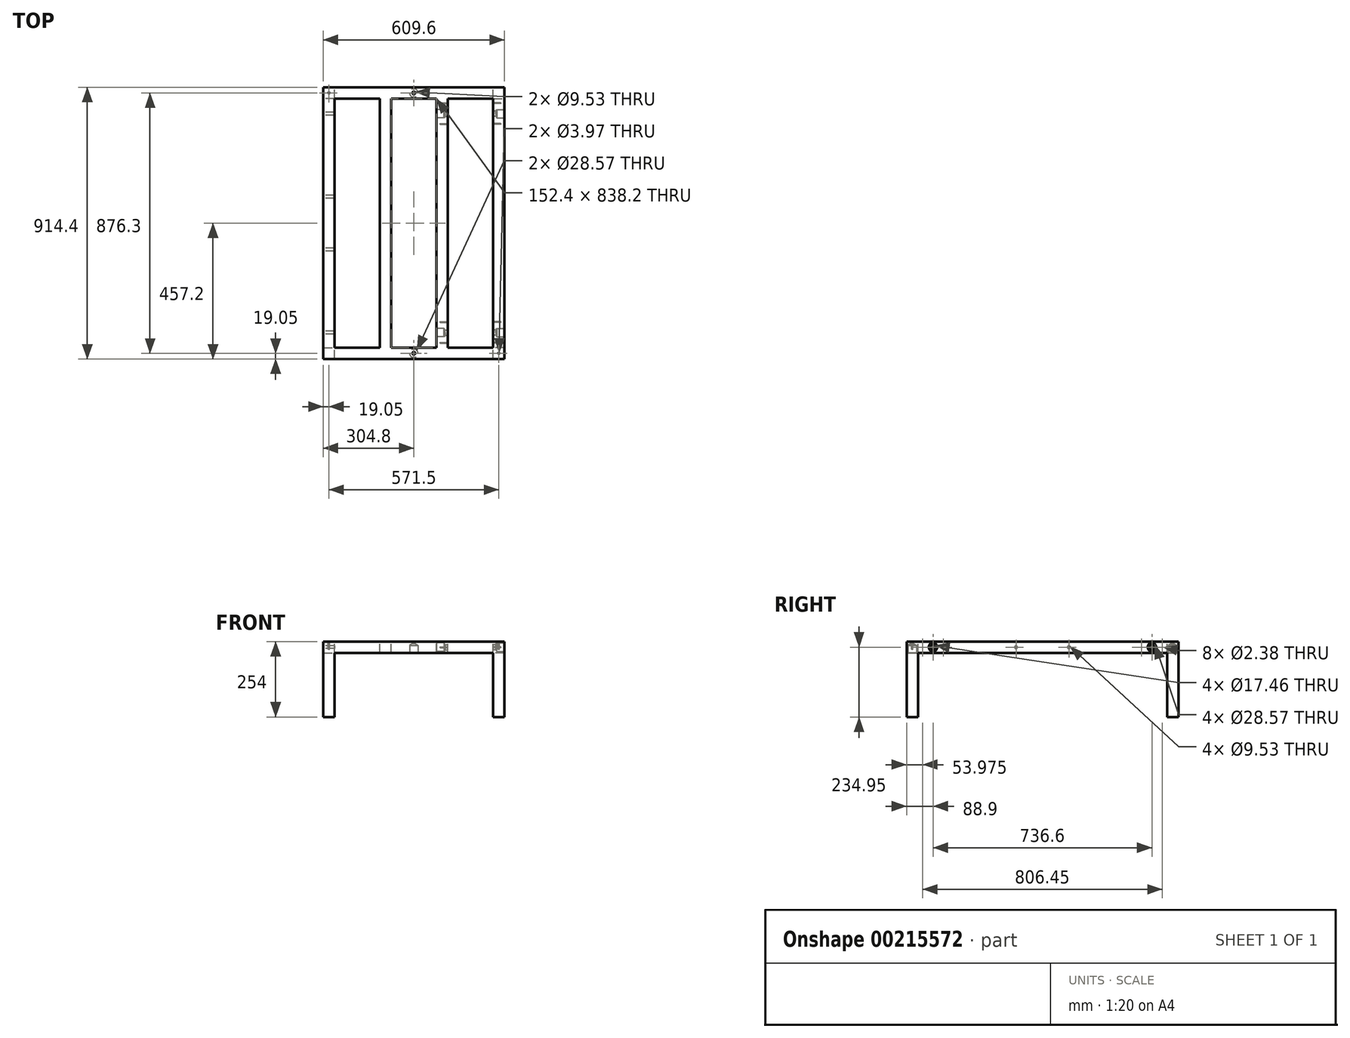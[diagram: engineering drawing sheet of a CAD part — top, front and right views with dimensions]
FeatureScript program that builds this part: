
annotation { "Feature Type Name" : "Feature", "Feature Type Description" : "" }
export const myFeature = defineFeature(function(context is Context, id is Id, definition is map)
    precondition{}
    {
        {
            var Q0;
            Q0=qCreatedBy(makeId("Top.planeOp"),FACE);
            var sketch = newSketch(context, id + "F0", { "sketchPlane" : qUnion([Q0])});
            skLineSegment(sketch, "E0.bottom", {"start": v(304.8, 457.2) * mm, "end": v(-304.8, 457.2) * mm});
            skLineSegment(sketch, "E0.top", {"start": v(304.8, -457.2) * mm, "end": v(-304.8, -457.2) * mm});
            skLineSegment(sketch, "E0.left", {"start": v(304.8, 457.2) * mm, "end": v(304.8, -457.2) * mm});
            skLineSegment(sketch, "E0.right", {"start": v(-304.8, 457.2) * mm, "end": v(-304.8, -457.2) * mm});
            skPoint(sketch, "E0.middle", {"position": v(0, 0) * mm});
            skLineSegment(sketch, "E1.bottom", {"start": v(266.7, 419.1) * mm, "end": v(114.3, 419.1) * mm});
            skLineSegment(sketch, "E1.top", {"start": v(266.7, -419.1) * mm, "end": v(114.3, -419.1) * mm});
            skLineSegment(sketch, "E1.left", {"start": v(266.7, 419.1) * mm, "end": v(266.7, -419.1) * mm});
            skLineSegment(sketch, "E1.right", {"start": v(-266.7, 419.1) * mm, "end": v(-266.7, -419.1) * mm});
            skLineSegment(sketch, "E2.0", {"start": v(-114.3, 419.1) * mm, "end": v(-114.3, -419.1) * mm});
            skLineSegment(sketch, "E3.0", {"start": v(-76.2, 419.1) * mm, "end": v(-76.2, -419.1) * mm});
            skLineSegment(sketch, "E4.0", {"start": v(76.2, 419.1) * mm, "end": v(76.2, -419.1) * mm});
            skLineSegment(sketch, "E5.0", {"start": v(114.3, 419.1) * mm, "end": v(114.3, -419.1) * mm});
            skLineSegment(sketch, "E6.trimOffspring", {"start": v(-114.3, 419.1) * mm, "end": v(-266.7, 419.1) * mm});
            skLineSegment(sketch, "E7.trimOffspring", {"start": v(76.2, 419.1) * mm, "end": v(-76.2, 419.1) * mm});
            skLineSegment(sketch, "E8.trimOffspring", {"start": v(-114.3, -419.1) * mm, "end": v(-266.7, -419.1) * mm});
            skLineSegment(sketch, "E9.trimOffspring", {"start": v(76.2, -419.1) * mm, "end": v(-76.2, -419.1) * mm});
            skSolve(sketch);
        }
        {
            var Q0;
            Q0=qSketchRegion(id+"F0",true);
            extrude(context, id + "F1", {"entities" : qUnion([Q0]), "oppositeDirection" : true, "depth" : 38.1 * mm});
        }
        {
            var Q0;
            Q0=makeQuery(id+"F1.opExtrude","CAP_FACE",FACE,{"disambiguationData":[OSD([sQuery(id+"F0.wireOp",EDGE,"E0.bottom"),sQuery(id+"F0.wireOp",EDGE,"E0.top"),sQuery(id+"F0.wireOp",EDGE,"E0.left"),sQuery(id+"F0.wireOp",EDGE,"E0.right"),sQuery(id+"F0.wireOp",EDGE,"E1.bottom"),sQuery(id+"F0.wireOp",EDGE,"E1.top"),sQuery(id+"F0.wireOp",EDGE,"E1.left"),sQuery(id+"F0.wireOp",EDGE,"E1.right"),sQuery(id+"F0.wireOp",EDGE,"E2.0"),sQuery(id+"F0.wireOp",EDGE,"E3.0"),sQuery(id+"F0.wireOp",EDGE,"E4.0"),sQuery(id+"F0.wireOp",EDGE,"E5.0"),sQuery(id+"F0.wireOp",EDGE,"E6.trimOffspring"),sQuery(id+"F0.wireOp",EDGE,"E7.trimOffspring"),sQuery(id+"F0.wireOp",EDGE,"E8.trimOffspring"),sQuery(id+"F0.wireOp",EDGE,"E9.trimOffspring")])],"isStart":false});
            var sketch = newSketch(context, id + "F2", { "sketchPlane" : qUnion([Q0])});
            skLineSegment(sketch, "E10.bottom", {"start": v(-266.7, -419.1) * mm, "end": v(-304.8, -419.1) * mm});
            skLineSegment(sketch, "E10.top", {"start": v(-266.7, -457.2) * mm, "end": v(-304.8, -457.2) * mm});
            skLineSegment(sketch, "E10.left", {"start": v(-266.7, -419.1) * mm, "end": v(-266.7, -457.2) * mm});
            skLineSegment(sketch, "E10.right", {"start": v(-304.8, -419.1) * mm, "end": v(-304.8, -457.2) * mm});
            skLineSegment(sketch, "E11.bottom", {"start": v(266.7, -419.1) * mm, "end": v(304.8, -419.1) * mm});
            skLineSegment(sketch, "E11.top", {"start": v(266.7, -457.2) * mm, "end": v(304.8, -457.2) * mm});
            skLineSegment(sketch, "E11.left", {"start": v(266.7, -419.1) * mm, "end": v(266.7, -457.2) * mm});
            skLineSegment(sketch, "E11.right", {"start": v(304.8, -419.1) * mm, "end": v(304.8, -457.2) * mm});
            skLineSegment(sketch, "E12.bottom", {"start": v(-304.8, 457.2) * mm, "end": v(-266.7, 457.2) * mm});
            skLineSegment(sketch, "E12.top", {"start": v(-304.8, 419.1) * mm, "end": v(-266.7, 419.1) * mm});
            skLineSegment(sketch, "E12.left", {"start": v(-304.8, 457.2) * mm, "end": v(-304.8, 419.1) * mm});
            skLineSegment(sketch, "E12.right", {"start": v(-266.7, 457.2) * mm, "end": v(-266.7, 419.1) * mm});
            skLineSegment(sketch, "E13.bottom", {"start": v(304.8, 457.2) * mm, "end": v(266.7, 457.2) * mm});
            skLineSegment(sketch, "E13.top", {"start": v(304.8, 419.1) * mm, "end": v(266.7, 419.1) * mm});
            skLineSegment(sketch, "E13.left", {"start": v(304.8, 457.2) * mm, "end": v(304.8, 419.1) * mm});
            skLineSegment(sketch, "E13.right", {"start": v(266.7, 457.2) * mm, "end": v(266.7, 419.1) * mm});
            skSolve(sketch);
        }
        {
            var Q0;
            Q0=makeQuery(id+"F2.imprint","IMPRINT",FACE,{"disambiguationData":[TD([[makeQuery(id+"F2.imprint","IMPRINT",EDGE,{"derivedFrom":sQuery(id+"F2.wireOp",EDGE,"E10.bottom")}),1.0]])]});
            var Q1;
            Q1=makeQuery(id+"F2.imprint","IMPRINT",FACE,{"disambiguationData":[TD([[makeQuery(id+"F2.imprint","IMPRINT",EDGE,{"derivedFrom":sQuery(id+"F2.wireOp",EDGE,"E11.bottom")}),-1.0]])]});
            var Q2;
            Q2=makeQuery(id+"F2.imprint","IMPRINT",FACE,{"disambiguationData":[TD([[makeQuery(id+"F2.imprint","IMPRINT",EDGE,{"derivedFrom":sQuery(id+"F2.wireOp",EDGE,"E13.bottom")}),1.0]])]});
            var Q3;
            Q3=makeQuery(id+"F2.imprint","IMPRINT",FACE,{"disambiguationData":[TD([[makeQuery(id+"F2.imprint","IMPRINT",EDGE,{"derivedFrom":sQuery(id+"F2.wireOp",EDGE,"E12.bottom")}),1.0]])]});
            extrude(context, id + "F3", {"entities" : qUnion([Q0, Q1, Q2, Q3]), "operationType" : NewBodyOperationType.ADD, "depth" : 215.9 * mm});
        }
        {
            var Q0;
            Q0=makeQuery(id+"F3.boolean.opBoolean","MERGE",FACE,{"derivedFrom":[makeQuery(id+"F1.opExtrude","SWEPT_FACE",FACE,{"disambiguationData":[OSD([sQuery(id+"F0.wireOp",EDGE,"E0.left")])]}),makeQuery(id+"F3.opExtrude","SWEPT_FACE",FACE,{"disambiguationData":[OSD([sQuery(id+"F2.wireOp",EDGE,"E11.right")])]}),makeQuery(id+"F3.opExtrude","SWEPT_FACE",FACE,{"disambiguationData":[OSD([sQuery(id+"F2.wireOp",EDGE,"E13.left")])]})]});
            var sketch = newSketch(context, id + "F4", { "sketchPlane" : qUnion([Q0])});
            skPoint(sketch, "E14", {"position": v(368.3, -19.05) * mm});
            skPoint(sketch, "E15", {"position": v(-368.3, -19.05) * mm});
            skPoint(sketch, "E16", {"position": v(-200.65, 261.37) * mm});
            skSolve(sketch);
        }
        {
            var Q0;
            Q0=makeQuery(id+"F1.opExtrude","SWEPT_FACE",FACE,{"disambiguationData":[OSD([sQuery(id+"F0.wireOp",EDGE,"E5.0")])]});
            var sketch = newSketch(context, id + "F5", { "sketchPlane" : qUnion([Q0])});
            skPoint(sketch, "E17.0", {"position": v(368.3, -19.05) * mm});
            skPoint(sketch, "E18.0", {"position": v(-368.3, -19.05) * mm});
            skSolve(sketch);
        }
        {
            var Q0;
            Q0=makeQuery(id+"F3.boolean.opBoolean","MERGE",FACE,{"derivedFrom":[makeQuery(id+"F1.opExtrude","SWEPT_FACE",FACE,{"disambiguationData":[OSD([sQuery(id+"F0.wireOp",EDGE,"E0.right")])]}),makeQuery(id+"F3.opExtrude","SWEPT_FACE",FACE,{"disambiguationData":[OSD([sQuery(id+"F2.wireOp",EDGE,"E10.right")])]}),makeQuery(id+"F3.opExtrude","SWEPT_FACE",FACE,{"disambiguationData":[OSD([sQuery(id+"F2.wireOp",EDGE,"E12.left")])]})]});
            var sketch = newSketch(context, id + "F6", { "sketchPlane" : qUnion([Q0])});
            skPoint(sketch, "E19.0", {"position": v(-368.3, -19.05) * mm});
            skPoint(sketch, "E20.0", {"position": v(-88.9, -19.05) * mm});
            skPoint(sketch, "E21.0", {"position": v(88.9, -19.05) * mm});
            skPoint(sketch, "E22.0", {"position": v(368.3, -19.05) * mm});
            skSolve(sketch);
        }
        {
            var Q0;
            Q0=makeQuery(id+"F1.opExtrude","SWEPT_FACE",FACE,{"disambiguationData":[OSD([sQuery(id+"F0.wireOp",EDGE,"E1.left")])]});
            var sketch = newSketch(context, id + "F7", { "sketchPlane" : qUnion([Q0])});
            skPoint(sketch, "E23.0", {"position": v(-368.3, -19.05) * mm});
            skPoint(sketch, "E24.0", {"position": v(368.3, -19.05) * mm});
            skPoint(sketch, "E25", {"position": v(403.23, -19.05) * mm});
            skPoint(sketch, "E26", {"position": v(333.38, -19.05) * mm});
            skLineSegment(sketch, "E27", {"start": v(368.3, -19.05) * mm, "end": v(368.3, 30.08) * mm, "construction": true});
            skPoint(sketch, "E28", {"position": v(-333.38, -19.05) * mm});
            skPoint(sketch, "E29", {"position": v(-403.23, -19.05) * mm});
            skLineSegment(sketch, "E30", {"start": v(-368.3, -19.05) * mm, "end": v(-368.3, 29.6) * mm, "construction": true});
            skSolve(sketch);
        }
        {
            var Q0;
            Q0=sQuery(id+"F4.wireOp",VERTEX,"E14");
            var Q1;
            Q1=sQuery(id+"F4.wireOp",VERTEX,"E15");
            var Q2;
            Q2=makeQuery(id+"F1.opExtrude","SWEPT_BODY",BODY,{"disambiguationData":[OSD([sQuery(id+"F0.wireOp",EDGE,"E0.bottom"),sQuery(id+"F0.wireOp",EDGE,"E0.top"),sQuery(id+"F0.wireOp",EDGE,"E0.left"),sQuery(id+"F0.wireOp",EDGE,"E0.right"),sQuery(id+"F0.wireOp",EDGE,"E1.bottom"),sQuery(id+"F0.wireOp",EDGE,"E1.top"),sQuery(id+"F0.wireOp",EDGE,"E1.left"),sQuery(id+"F0.wireOp",EDGE,"E1.right"),sQuery(id+"F0.wireOp",EDGE,"E2.0"),sQuery(id+"F0.wireOp",EDGE,"E3.0"),sQuery(id+"F0.wireOp",EDGE,"E4.0"),sQuery(id+"F0.wireOp",EDGE,"E5.0"),sQuery(id+"F0.wireOp",EDGE,"E6.trimOffspring"),sQuery(id+"F0.wireOp",EDGE,"E7.trimOffspring"),sQuery(id+"F0.wireOp",EDGE,"E8.trimOffspring"),sQuery(id+"F0.wireOp",EDGE,"E9.trimOffspring")])]});
            hole(context, id + "F8", {"style" : HoleStyle.SIMPLE, "endStyle" : HoleEndStyle.BLIND, "holeDiameter" : 28.57 * mm, "holeDepth" : 25.4 * mm, "locations" : qUnion([Q0, Q1]), "scope" : qUnion([Q2])});
        }
        {
            var Q0;
            Q0=sQuery(id+"F5.wireOp",VERTEX,"E17.0");
            var Q1;
            Q1=sQuery(id+"F5.wireOp",VERTEX,"E18.0");
            var Q2;
            Q2=makeQuery(id+"F1.opExtrude","SWEPT_BODY",BODY,{"disambiguationData":[OSD([sQuery(id+"F0.wireOp",EDGE,"E0.bottom"),sQuery(id+"F0.wireOp",EDGE,"E0.top"),sQuery(id+"F0.wireOp",EDGE,"E0.left"),sQuery(id+"F0.wireOp",EDGE,"E0.right"),sQuery(id+"F0.wireOp",EDGE,"E1.bottom"),sQuery(id+"F0.wireOp",EDGE,"E1.top"),sQuery(id+"F0.wireOp",EDGE,"E1.left"),sQuery(id+"F0.wireOp",EDGE,"E1.right"),sQuery(id+"F0.wireOp",EDGE,"E2.0"),sQuery(id+"F0.wireOp",EDGE,"E3.0"),sQuery(id+"F0.wireOp",EDGE,"E4.0"),sQuery(id+"F0.wireOp",EDGE,"E5.0"),sQuery(id+"F0.wireOp",EDGE,"E6.trimOffspring"),sQuery(id+"F0.wireOp",EDGE,"E7.trimOffspring"),sQuery(id+"F0.wireOp",EDGE,"E8.trimOffspring"),sQuery(id+"F0.wireOp",EDGE,"E9.trimOffspring")])]});
            hole(context, id + "F9", {"style" : HoleStyle.SIMPLE, "endStyle" : HoleEndStyle.BLIND, "holeDiameter" : 17.46 * mm, "holeDepth" : 25.4 * mm, "locations" : qUnion([Q0, Q1]), "scope" : qUnion([Q2])});
        }
        {
            var Q0;
            Q0=sQuery(id+"F7.wireOp",VERTEX,"E23.0");
            var Q1;
            Q1=sQuery(id+"F7.wireOp",VERTEX,"E24.0");
            var Q2;
            Q2=makeQuery(id+"F1.opExtrude","SWEPT_BODY",BODY,{"disambiguationData":[OSD([sQuery(id+"F0.wireOp",EDGE,"E0.bottom"),sQuery(id+"F0.wireOp",EDGE,"E0.top"),sQuery(id+"F0.wireOp",EDGE,"E0.left"),sQuery(id+"F0.wireOp",EDGE,"E0.right"),sQuery(id+"F0.wireOp",EDGE,"E1.bottom"),sQuery(id+"F0.wireOp",EDGE,"E1.top"),sQuery(id+"F0.wireOp",EDGE,"E1.left"),sQuery(id+"F0.wireOp",EDGE,"E1.right"),sQuery(id+"F0.wireOp",EDGE,"E2.0"),sQuery(id+"F0.wireOp",EDGE,"E3.0"),sQuery(id+"F0.wireOp",EDGE,"E4.0"),sQuery(id+"F0.wireOp",EDGE,"E5.0"),sQuery(id+"F0.wireOp",EDGE,"E6.trimOffspring"),sQuery(id+"F0.wireOp",EDGE,"E7.trimOffspring"),sQuery(id+"F0.wireOp",EDGE,"E8.trimOffspring"),sQuery(id+"F0.wireOp",EDGE,"E9.trimOffspring")])]});
            hole(context, id + "F10", {"style" : HoleStyle.SIMPLE, "endStyle" : HoleEndStyle.BLIND, "holeDiameter" : 17.46 * mm, "holeDepth" : 25.4 * mm, "locations" : qUnion([Q0, Q1]), "scope" : qUnion([Q2])});
        }
        {
            var Q0;
            Q0=makeQuery(id+"F1.opExtrude","SWEPT_FACE",FACE,{"disambiguationData":[OSD([sQuery(id+"F0.wireOp",EDGE,"E4.0")])]});
            var sketch = newSketch(context, id + "F11", { "sketchPlane" : qUnion([Q0])});
            skPoint(sketch, "E31.0", {"position": v(-368.3, -19.05) * mm});
            skPoint(sketch, "E32.0", {"position": v(368.3, -19.05) * mm});
            skSolve(sketch);
        }
        {
            var Q0;
            Q0=sQuery(id+"F11.wireOp",VERTEX,"E31.0");
            var Q1;
            Q1=sQuery(id+"F11.wireOp",VERTEX,"E32.0");
            var Q2;
            Q2=makeQuery(id+"F1.opExtrude","SWEPT_BODY",BODY,{"disambiguationData":[OSD([sQuery(id+"F0.wireOp",EDGE,"E0.bottom"),sQuery(id+"F0.wireOp",EDGE,"E0.top"),sQuery(id+"F0.wireOp",EDGE,"E0.left"),sQuery(id+"F0.wireOp",EDGE,"E0.right"),sQuery(id+"F0.wireOp",EDGE,"E1.bottom"),sQuery(id+"F0.wireOp",EDGE,"E1.top"),sQuery(id+"F0.wireOp",EDGE,"E1.left"),sQuery(id+"F0.wireOp",EDGE,"E1.right"),sQuery(id+"F0.wireOp",EDGE,"E2.0"),sQuery(id+"F0.wireOp",EDGE,"E3.0"),sQuery(id+"F0.wireOp",EDGE,"E4.0"),sQuery(id+"F0.wireOp",EDGE,"E5.0"),sQuery(id+"F0.wireOp",EDGE,"E6.trimOffspring"),sQuery(id+"F0.wireOp",EDGE,"E7.trimOffspring"),sQuery(id+"F0.wireOp",EDGE,"E8.trimOffspring"),sQuery(id+"F0.wireOp",EDGE,"E9.trimOffspring")])]});
            hole(context, id + "F12", {"style" : HoleStyle.SIMPLE, "endStyle" : HoleEndStyle.BLIND, "holeDiameter" : 28.57 * mm, "holeDepth" : 25.4 * mm, "locations" : qUnion([Q0, Q1]), "scope" : qUnion([Q2])});
        }
        {
            var Q0;
            Q0=sQuery(id+"F6.wireOp",VERTEX,"E19.0");
            var Q1;
            Q1=sQuery(id+"F6.wireOp",VERTEX,"E20.0");
            var Q2;
            Q2=sQuery(id+"F6.wireOp",VERTEX,"E21.0");
            var Q3;
            Q3=sQuery(id+"F6.wireOp",VERTEX,"E22.0");
            var Q4;
            Q4=makeQuery(id+"F1.opExtrude","SWEPT_BODY",BODY,{"disambiguationData":[OSD([sQuery(id+"F0.wireOp",EDGE,"E0.bottom"),sQuery(id+"F0.wireOp",EDGE,"E0.top"),sQuery(id+"F0.wireOp",EDGE,"E0.left"),sQuery(id+"F0.wireOp",EDGE,"E0.right"),sQuery(id+"F0.wireOp",EDGE,"E1.bottom"),sQuery(id+"F0.wireOp",EDGE,"E1.top"),sQuery(id+"F0.wireOp",EDGE,"E1.left"),sQuery(id+"F0.wireOp",EDGE,"E1.right"),sQuery(id+"F0.wireOp",EDGE,"E2.0"),sQuery(id+"F0.wireOp",EDGE,"E3.0"),sQuery(id+"F0.wireOp",EDGE,"E4.0"),sQuery(id+"F0.wireOp",EDGE,"E5.0"),sQuery(id+"F0.wireOp",EDGE,"E6.trimOffspring"),sQuery(id+"F0.wireOp",EDGE,"E7.trimOffspring"),sQuery(id+"F0.wireOp",EDGE,"E8.trimOffspring"),sQuery(id+"F0.wireOp",EDGE,"E9.trimOffspring")])]});
            hole(context, id + "F13", {"style" : HoleStyle.SIMPLE, "endStyle" : HoleEndStyle.BLIND, "holeDiameter" : 9.52 * mm, "holeDepth" : 50.8 * mm, "locations" : qUnion([Q0, Q1, Q2, Q3]), "scope" : qUnion([Q4])});
        }
        {
            var Q0;
            Q0=makeQuery(id+"F1.opExtrude","SWEPT_FACE",FACE,{"disambiguationData":[OSD([sQuery(id+"F0.wireOp",EDGE,"E5.0")])]});
            var sketch = newSketch(context, id + "F14", { "sketchPlane" : qUnion([Q0])});
            skPoint(sketch, "E33.0", {"position": v(-403.23, -19.05) * mm});
            skPoint(sketch, "E34.0", {"position": v(-333.38, -19.05) * mm});
            skPoint(sketch, "E35.0", {"position": v(333.38, -19.05) * mm});
            skPoint(sketch, "E36.0", {"position": v(403.23, -19.05) * mm});
            skSolve(sketch);
        }
        {
            var Q0;
            Q0=sQuery(id+"F14.wireOp",VERTEX,"E33.0");
            var Q1;
            Q1=sQuery(id+"F14.wireOp",VERTEX,"E34.0");
            var Q2;
            Q2=sQuery(id+"F14.wireOp",VERTEX,"E35.0");
            var Q3;
            Q3=sQuery(id+"F14.wireOp",VERTEX,"E36.0");
            var Q4;
            Q4=sQuery(id+"F7.wireOp",VERTEX,"E25");
            var Q5;
            Q5=sQuery(id+"F7.wireOp",VERTEX,"E26");
            var Q6;
            Q6=sQuery(id+"F7.wireOp",VERTEX,"E28");
            var Q7;
            Q7=sQuery(id+"F7.wireOp",VERTEX,"E29");
            var Q8;
            Q8=makeQuery(id+"F1.opExtrude","SWEPT_BODY",BODY,{"disambiguationData":[OSD([sQuery(id+"F0.wireOp",EDGE,"E0.bottom"),sQuery(id+"F0.wireOp",EDGE,"E0.top"),sQuery(id+"F0.wireOp",EDGE,"E0.left"),sQuery(id+"F0.wireOp",EDGE,"E0.right"),sQuery(id+"F0.wireOp",EDGE,"E1.bottom"),sQuery(id+"F0.wireOp",EDGE,"E1.top"),sQuery(id+"F0.wireOp",EDGE,"E1.left"),sQuery(id+"F0.wireOp",EDGE,"E1.right"),sQuery(id+"F0.wireOp",EDGE,"E2.0"),sQuery(id+"F0.wireOp",EDGE,"E3.0"),sQuery(id+"F0.wireOp",EDGE,"E4.0"),sQuery(id+"F0.wireOp",EDGE,"E5.0"),sQuery(id+"F0.wireOp",EDGE,"E6.trimOffspring"),sQuery(id+"F0.wireOp",EDGE,"E7.trimOffspring"),sQuery(id+"F0.wireOp",EDGE,"E8.trimOffspring"),sQuery(id+"F0.wireOp",EDGE,"E9.trimOffspring")])]});
            hole(context, id + "F15", {"style" : HoleStyle.SIMPLE, "endStyle" : HoleEndStyle.BLIND, "holeDiameter" : 2.38 * mm, "holeDepth" : 25.4 * mm, "locations" : qUnion([Q0, Q1, Q2, Q3, Q4, Q5, Q6, Q7]), "scope" : qUnion([Q8])});
        }
        {
            var Q0;
            Q0=makeQuery(id+"F1.opExtrude","CAP_FACE",FACE,{"disambiguationData":[OSD([sQuery(id+"F0.wireOp",EDGE,"E0.bottom"),sQuery(id+"F0.wireOp",EDGE,"E0.top"),sQuery(id+"F0.wireOp",EDGE,"E0.left"),sQuery(id+"F0.wireOp",EDGE,"E0.right"),sQuery(id+"F0.wireOp",EDGE,"E1.bottom"),sQuery(id+"F0.wireOp",EDGE,"E1.top"),sQuery(id+"F0.wireOp",EDGE,"E1.left"),sQuery(id+"F0.wireOp",EDGE,"E1.right"),sQuery(id+"F0.wireOp",EDGE,"E2.0"),sQuery(id+"F0.wireOp",EDGE,"E3.0"),sQuery(id+"F0.wireOp",EDGE,"E4.0"),sQuery(id+"F0.wireOp",EDGE,"E5.0"),sQuery(id+"F0.wireOp",EDGE,"E6.trimOffspring"),sQuery(id+"F0.wireOp",EDGE,"E7.trimOffspring"),sQuery(id+"F0.wireOp",EDGE,"E8.trimOffspring"),sQuery(id+"F0.wireOp",EDGE,"E9.trimOffspring")])],"isStart":true});
            var sketch = newSketch(context, id + "F16", { "sketchPlane" : qUnion([Q0])});
            skPoint(sketch, "E37", {"position": v(285.75, -438.15) * mm});
            skPoint(sketch, "E38", {"position": v(-285.75, 438.15) * mm});
            skPoint(sketch, "E39.positionSnap0", {"position": v(190.5, -419.1) * mm});
            skPoint(sketch, "E40.positionSnap0", {"position": v(190.5, 419.1) * mm});
            skPoint(sketch, "E41", {"position": v(0, -438.15) * mm});
            skPoint(sketch, "E41.positionSnap0", {"position": v(0, -419.1) * mm});
            skPoint(sketch, "E42", {"position": v(0, 438.15) * mm});
            skPoint(sketch, "E42.positionSnap0", {"position": v(0, 419.1) * mm});
            skSolve(sketch);
        }
        {
            var Q0;
            Q0=sQuery(id+"F16.wireOp",VERTEX,"E38");
            var Q1;
            Q1=sQuery(id+"F16.wireOp",VERTEX,"E37");
            var Q2;
            Q2=makeQuery(id+"F1.opExtrude","SWEPT_BODY",BODY,{"disambiguationData":[OSD([sQuery(id+"F0.wireOp",EDGE,"E0.bottom"),sQuery(id+"F0.wireOp",EDGE,"E0.top"),sQuery(id+"F0.wireOp",EDGE,"E0.left"),sQuery(id+"F0.wireOp",EDGE,"E0.right"),sQuery(id+"F0.wireOp",EDGE,"E1.bottom"),sQuery(id+"F0.wireOp",EDGE,"E1.top"),sQuery(id+"F0.wireOp",EDGE,"E1.left"),sQuery(id+"F0.wireOp",EDGE,"E1.right"),sQuery(id+"F0.wireOp",EDGE,"E2.0"),sQuery(id+"F0.wireOp",EDGE,"E3.0"),sQuery(id+"F0.wireOp",EDGE,"E4.0"),sQuery(id+"F0.wireOp",EDGE,"E5.0"),sQuery(id+"F0.wireOp",EDGE,"E6.trimOffspring"),sQuery(id+"F0.wireOp",EDGE,"E7.trimOffspring"),sQuery(id+"F0.wireOp",EDGE,"E8.trimOffspring"),sQuery(id+"F0.wireOp",EDGE,"E9.trimOffspring")])]});
            hole(context, id + "F17", {"style" : HoleStyle.SIMPLE, "endStyle" : HoleEndStyle.BLIND, "holeDiameter" : 3.97 * mm, "holeDepth" : 25.4 * mm, "locations" : qUnion([Q0, Q1]), "scope" : qUnion([Q2])});
        }
        {
            var Q0;
            Q0=sQuery(id+"F16.wireOp",VERTEX,"E42");
            var Q1;
            Q1=sQuery(id+"F16.wireOp",VERTEX,"E41");
            var Q2;
            Q2=makeQuery(id+"F1.opExtrude","SWEPT_BODY",BODY,{"disambiguationData":[OSD([sQuery(id+"F0.wireOp",EDGE,"E0.bottom"),sQuery(id+"F0.wireOp",EDGE,"E0.top"),sQuery(id+"F0.wireOp",EDGE,"E0.left"),sQuery(id+"F0.wireOp",EDGE,"E0.right"),sQuery(id+"F0.wireOp",EDGE,"E1.bottom"),sQuery(id+"F0.wireOp",EDGE,"E1.top"),sQuery(id+"F0.wireOp",EDGE,"E1.left"),sQuery(id+"F0.wireOp",EDGE,"E1.right"),sQuery(id+"F0.wireOp",EDGE,"E2.0"),sQuery(id+"F0.wireOp",EDGE,"E3.0"),sQuery(id+"F0.wireOp",EDGE,"E4.0"),sQuery(id+"F0.wireOp",EDGE,"E5.0"),sQuery(id+"F0.wireOp",EDGE,"E6.trimOffspring"),sQuery(id+"F0.wireOp",EDGE,"E7.trimOffspring"),sQuery(id+"F0.wireOp",EDGE,"E8.trimOffspring"),sQuery(id+"F0.wireOp",EDGE,"E9.trimOffspring")])]});
            hole(context, id + "F18", {"style" : HoleStyle.SIMPLE, "endStyle" : HoleEndStyle.BLIND, "holeDiameter" : 9.52 * mm, "holeDepth" : 25.4 * mm, "locations" : qUnion([Q0, Q1]), "scope" : qUnion([Q2])});
        }
        {
            var Q0;
            {var subQ0=sQuery(id+"F0.wireOp",EDGE,"E0.bottom");var subQ1=sQuery(id+"F0.wireOp",EDGE,"E0.top");var subQ2=sQuery(id+"F0.wireOp",EDGE,"E7.trimOffspring");var subQ3=sQuery(id+"F0.wireOp",EDGE,"E6.trimOffspring");var subQ4=sQuery(id+"F0.wireOp",EDGE,"E1.bottom");var subQ5=sQuery(id+"F0.wireOp",EDGE,"E9.trimOffspring");var subQ6=sQuery(id+"F0.wireOp",EDGE,"E2.0");var subQ7=sQuery(id+"F0.wireOp",EDGE,"E5.0");var subQ8=sQuery(id+"F0.wireOp",EDGE,"E8.trimOffspring");var subQ9=sQuery(id+"F0.wireOp",EDGE,"E4.0");var subQ10=sQuery(id+"F0.wireOp",EDGE,"E3.0");var subQ11=sQuery(id+"F0.wireOp",EDGE,"E1.right");var subQ12=sQuery(id+"F0.wireOp",EDGE,"E1.left");var subQ13=sQuery(id+"F0.wireOp",EDGE,"E1.top");var subQ14=makeQuery(id+"F1.opExtrude","CAP_FACE",FACE,{"disambiguationData":[OSD([subQ0,subQ1,sQuery(id+"F0.wireOp",EDGE,"E0.left"),sQuery(id+"F0.wireOp",EDGE,"E0.right"),subQ4,subQ13,subQ12,subQ11,subQ6,subQ10,subQ9,subQ7,subQ3,subQ2,subQ8,subQ5])],"isStart":false});Q0=makeQuery(id+"F3.boolean.opBoolean","SPLIT",FACE,{"disambiguationData":[TD([makeQuery(id+"F1.opExtrude","SWEPT_FACE",FACE,{"disambiguationData":[OSD([subQ0])]})])],"derivedFrom":subQ14});}
            var sketch = newSketch(context, id + "F19", { "sketchPlane" : qUnion([Q0])});
            skPoint(sketch, "E43.0", {"position": v(0, 438.15) * mm});
            skPoint(sketch, "E44.0", {"position": v(0, -438.15) * mm});
            skSolve(sketch);
        }
        {
            var Q0;
            Q0=sQuery(id+"F19.wireOp",VERTEX,"E43.0");
            var Q1;
            Q1=sQuery(id+"F19.wireOp",VERTEX,"E44.0");
            var Q2;
            Q2=makeQuery(id+"F1.opExtrude","SWEPT_BODY",BODY,{"disambiguationData":[OSD([sQuery(id+"F0.wireOp",EDGE,"E0.bottom"),sQuery(id+"F0.wireOp",EDGE,"E0.top"),sQuery(id+"F0.wireOp",EDGE,"E0.left"),sQuery(id+"F0.wireOp",EDGE,"E0.right"),sQuery(id+"F0.wireOp",EDGE,"E1.bottom"),sQuery(id+"F0.wireOp",EDGE,"E1.top"),sQuery(id+"F0.wireOp",EDGE,"E1.left"),sQuery(id+"F0.wireOp",EDGE,"E1.right"),sQuery(id+"F0.wireOp",EDGE,"E2.0"),sQuery(id+"F0.wireOp",EDGE,"E3.0"),sQuery(id+"F0.wireOp",EDGE,"E4.0"),sQuery(id+"F0.wireOp",EDGE,"E5.0"),sQuery(id+"F0.wireOp",EDGE,"E6.trimOffspring"),sQuery(id+"F0.wireOp",EDGE,"E7.trimOffspring"),sQuery(id+"F0.wireOp",EDGE,"E8.trimOffspring"),sQuery(id+"F0.wireOp",EDGE,"E9.trimOffspring")])]});
            hole(context, id + "F20", {"style" : HoleStyle.SIMPLE, "endStyle" : HoleEndStyle.BLIND, "holeDiameter" : 28.57 * mm, "holeDepth" : 25.4 * mm, "locations" : qUnion([Q0, Q1]), "scope" : qUnion([Q2])});
        }
        {
            var Q0;
            Q0=makeQuery(id+"F1.opExtrude","SWEPT_BODY",BODY,{"disambiguationData":[OSD([sQuery(id+"F0.wireOp",EDGE,"E0.bottom"),sQuery(id+"F0.wireOp",EDGE,"E0.top"),sQuery(id+"F0.wireOp",EDGE,"E0.left"),sQuery(id+"F0.wireOp",EDGE,"E0.right"),sQuery(id+"F0.wireOp",EDGE,"E1.bottom"),sQuery(id+"F0.wireOp",EDGE,"E1.top"),sQuery(id+"F0.wireOp",EDGE,"E1.left"),sQuery(id+"F0.wireOp",EDGE,"E1.right"),sQuery(id+"F0.wireOp",EDGE,"E2.0"),sQuery(id+"F0.wireOp",EDGE,"E3.0"),sQuery(id+"F0.wireOp",EDGE,"E4.0"),sQuery(id+"F0.wireOp",EDGE,"E5.0"),sQuery(id+"F0.wireOp",EDGE,"E6.trimOffspring"),sQuery(id+"F0.wireOp",EDGE,"E7.trimOffspring"),sQuery(id+"F0.wireOp",EDGE,"E8.trimOffspring"),sQuery(id+"F0.wireOp",EDGE,"E9.trimOffspring")])]});
            transform(context, id + "F21", {"entities" : qUnion([Q0]), "transformType" : TransformType.TRANSLATION_3D, "dx" : 0 * mm, "dy" : 0 * mm, "dz" : 0 * mm, "makeCopy" : true});
        }
        {
            var Q0;
            Q0=makeQuery(id+"F21.opPattern","COPY",BODY,{"derivedFrom":makeQuery(id+"F1.opExtrude","SWEPT_BODY",BODY,{"disambiguationData":[OSD([sQuery(id+"F0.wireOp",EDGE,"E0.bottom"),sQuery(id+"F0.wireOp",EDGE,"E0.top"),sQuery(id+"F0.wireOp",EDGE,"E0.left"),sQuery(id+"F0.wireOp",EDGE,"E0.right"),sQuery(id+"F0.wireOp",EDGE,"E1.bottom"),sQuery(id+"F0.wireOp",EDGE,"E1.top"),sQuery(id+"F0.wireOp",EDGE,"E1.left"),sQuery(id+"F0.wireOp",EDGE,"E1.right"),sQuery(id+"F0.wireOp",EDGE,"E2.0"),sQuery(id+"F0.wireOp",EDGE,"E3.0"),sQuery(id+"F0.wireOp",EDGE,"E4.0"),sQuery(id+"F0.wireOp",EDGE,"E5.0"),sQuery(id+"F0.wireOp",EDGE,"E6.trimOffspring"),sQuery(id+"F0.wireOp",EDGE,"E7.trimOffspring"),sQuery(id+"F0.wireOp",EDGE,"E8.trimOffspring"),sQuery(id+"F0.wireOp",EDGE,"E9.trimOffspring")])]}),"instanceName":"1"});
            deleteBodies(context, id + "F22", {"entities" : qUnion([Q0])});
        }
    });
